# Revit family: Furniture_Office-Chairs_Flokk_Giroflex-353_Conference
name_source: partatom
category: Furniture
units: mm (PartAtom-declared; Revit-internal decimal feet)

## family parameters
Always vertical = Yes
Cut with Voids When Loaded = No
OmniClass Number = 23.40.20.14.14.11
OmniClass Title = Chairs
Room Calculation Point = No
Shared = No
Work Plane-Based = No

## types (1)
- Giroflex 353 Conference
    AssetType = Movable
    BIMObjectName = Furniture_Office-Chairs_Flokk_Giroflex-353_Conference
    Brand = Flokk
    Category = Giroflex
    Color = Various
    Cost = 0 $
    Default Elevation = 0 mm  [stored 0 ft]
    Description = The giroflex 353 conference chair makes it easy for everyone. In tiring meetings too. With the chairs eye-cathing and winning design that can beconfigurated in the wide range of colours this chair has a lot going for it, for a long while!

This version is delivered with a refreshing backrest in mesh. You can also configurate with a version with a comfortable upholstered backrest for a more airy sensation. Thanks to an ideal back design and ergonomic shape, the 353 confrence chair will, in both cases, not only go along with all possible changes but helps and supports in any situation too.
    Designer = Paolo Fancelli
    DurationUnit = Year
    IfcExportAs = IfcFurnishingElementType
    IfcExportType = CHAIR
    LowestSeatingHeight = 500 mm  [stored 1.64042 ft]
    MainColor = Various
    Manufacturer = Flokk
    ManufacturerName = Flokk
    ManufacturerURL = https://www.flokk.com
    Material = Plastic, Metal and Textile
    Model = Giroflex 353 Conference
    ModelNumber = 353-3018
    NBSDescription = Stacking chairs
    NBSReference = 45-35-20/355
    Name = Giroflex-353_Conference
    NominalDepth = 570 mm
    NominalLength = 480 mm
    OfficeChairQuaternaryMaterial = Black RAL 9005
    ProductDatasheet = https://flokkplatformprod.blob.core.windows.net
    ProductInformation = The giroflex 353 family contains chairs for the personal touch, without screaming too loud. A soft, round design and a high delivery on ergonomic comfort.
    SeatingHeight = 500 mm  [stored 1.64042 ft]
    Shape = Sculptured
    Size = 480x570x940 mm
    URL = https://store.flokk.com
    Uniclass2 = Pr_40_50_12_51
    Uniclass2015Description = Meeting room chairs
    Uniclass2015Reference = Pr_40_50_12_51
    Version = 1
    VersionDate = 10/01/2022
    WarrantyDurationUnit = Year

note: [stored X ft] marks values corroborated as IEEE doubles in the binary element streams (Revit-internal decimal feet)

## geometry (parser evidence)
native form markers: Sweep x7
no freeform markers — native parametric forms only
